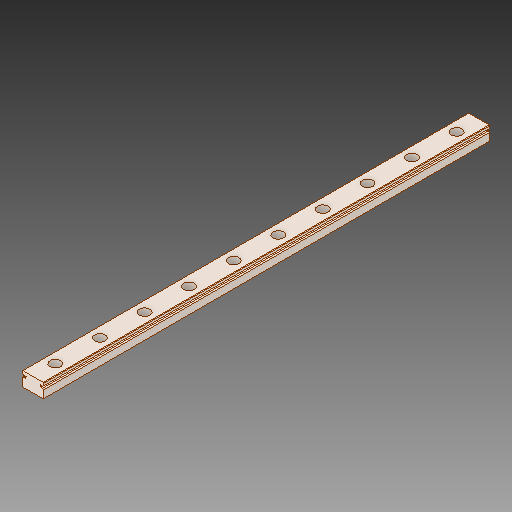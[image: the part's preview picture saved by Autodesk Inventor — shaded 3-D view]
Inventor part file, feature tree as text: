
AUTODESK INVENTOR PART (.ipt)
format: ipt  version: 2018 (Build 220112000, 112)  size: 175,616 bytes
history: native  units: in
note: dims shown in document units (in); Inventor stores cm internally (conversion verified against a paired STEP export)
features: other x1, extrude x1, sketch x1
ambient origin geometry x8: Origin, YZ Plane, XZ Plane, XY Plane, X Axis, Y Axis, Z Axis, Center Point
bodies: Solid1 (feature_tree)
feature tree (3):
  other  "Pattern1"
  extrude  "Extrusion1"  Depth=0.7874in
  sketch  "Sketch1"  dims[d0=5.9055in d1=0.7874in d2=0.3937in d3=0.0in]
